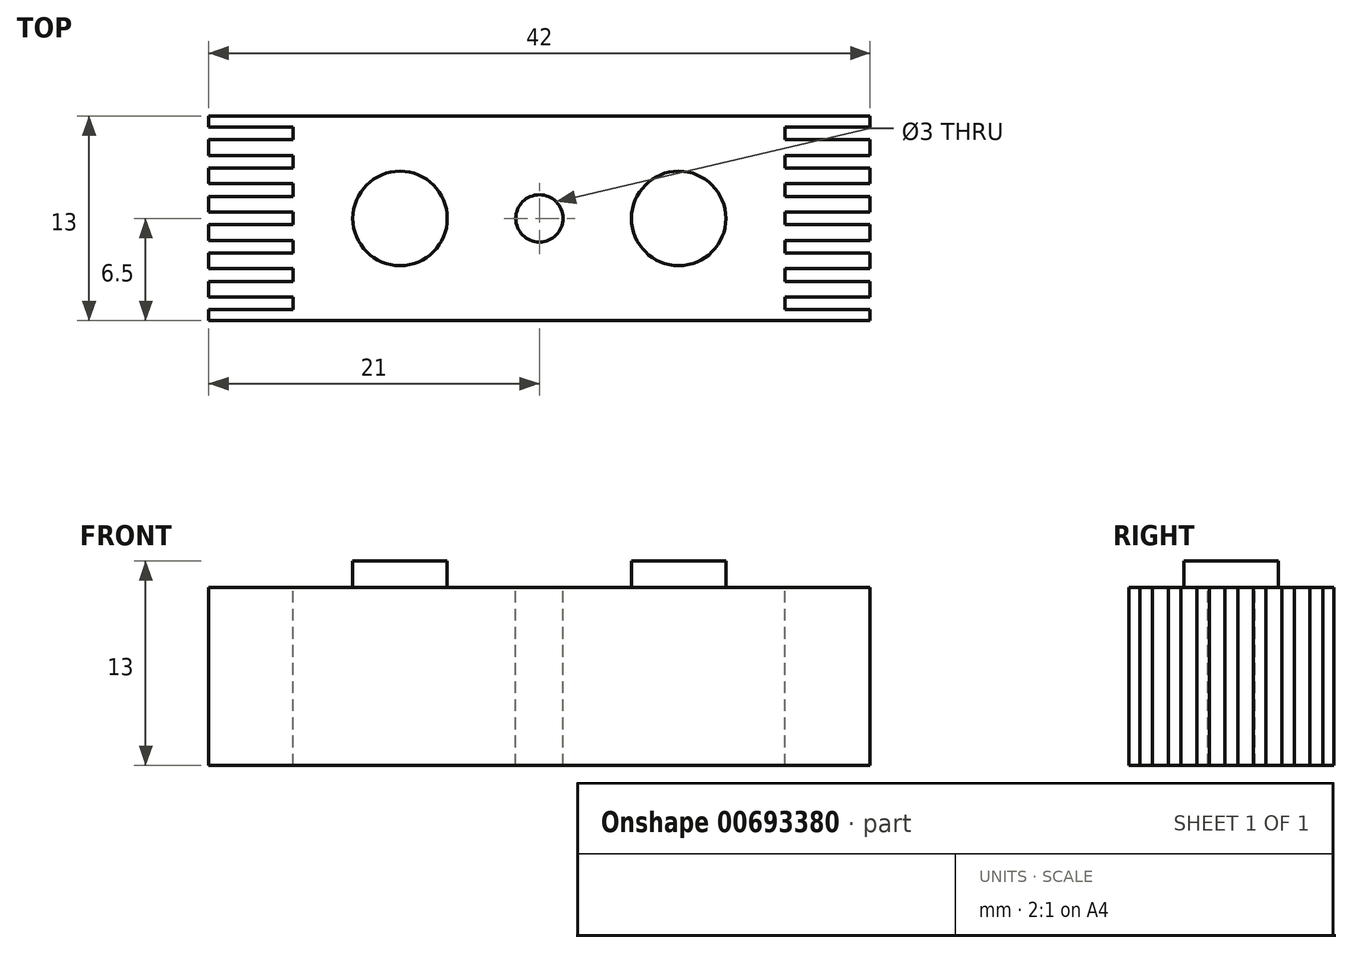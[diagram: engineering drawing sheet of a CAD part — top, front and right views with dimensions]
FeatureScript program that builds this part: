
annotation { "Feature Type Name" : "Feature", "Feature Type Description" : "" }
export const myFeature = defineFeature(function(context is Context, id is Id, definition is map)
    precondition{}
    {
        {
            var Q0;
            Q0=qCreatedBy(makeId("Top.planeOp"),FACE);
            var sketch = newSketch(context, id + "F0", { "sketchPlane" : qUnion([Q0])});
            skLineSegment(sketch, "E0.bottom", {"start": v(-21, 6.5) * mm, "end": v(21, 6.5) * mm});
            skLineSegment(sketch, "E0.top", {"start": v(-21, -6.5) * mm, "end": v(21, -6.5) * mm});
            skLineSegment(sketch, "E0.left", {"start": v(-21, 6.5) * mm, "end": v(-21, -6.5) * mm});
            skLineSegment(sketch, "E0.right", {"start": v(21, 6.5) * mm, "end": v(21, -6.5) * mm});
            skSolve(sketch);
        }
        {
            var Q0;
            Q0=makeQuery(id+"F0.imprint","IMPRINT",FACE,{"disambiguationData":[TD([[makeQuery(id+"F0.imprint","IMPRINT",EDGE,{"derivedFrom":sQuery(id+"F0.wireOp",EDGE,"E0.bottom")}),-1.0]])]});
            extrude(context, id + "F1", {"entities" : qUnion([Q0]), "depth" : 13 * mm, "offsetDistance" : 25 * mm});
        }
        {
            var Q0;
            Q0=makeQuery(id+"F1.opExtrude","CAP_FACE",FACE,{"disambiguationData":[OSD([sQuery(id+"F0.wireOp",EDGE,"E0.bottom"),sQuery(id+"F0.wireOp",EDGE,"E0.top"),sQuery(id+"F0.wireOp",EDGE,"E0.left"),sQuery(id+"F0.wireOp",EDGE,"E0.right")])],"isStart":false});
            var sketch = newSketch(context, id + "F2", { "sketchPlane" : qUnion([Q0])});
            skCircle(sketch, "E1", {"center": v(-8.85, 0) * mm, "radius": 3 * mm});
            skCircle(sketch, "E2", {"center": v(8.85, 0) * mm, "radius": 3 * mm});
            skSolve(sketch);
        }
        {
            var Q0;
            Q0=makeQuery(id+"F2.imprint","IMPRINT",FACE,{"disambiguationData":[TD([[makeQuery(id+"F2.imprint","IMPRINT",EDGE,{"derivedFrom":sQuery(id+"F2.wireOp",EDGE,"E1")}),-1.0]])]});
            extrude(context, id + "F3", {"entities" : qUnion([Q0]), "operationType" : NewBodyOperationType.REMOVE, "oppositeDirection" : true, "depth" : 1.7 * mm, "offsetDistance" : 25 * mm});
        }
        {
            var Q0;
            Q0=makeQuery(id+"F3.boolean.opBoolean","COPY",FACE,{"derivedFrom":makeQuery(id+"F3.opExtrude","CAP_FACE",FACE,{"disambiguationData":[OSD([sQuery(id+"F0.wireOp",EDGE,"E0.bottom"),sQuery(id+"F0.wireOp",EDGE,"E0.top"),sQuery(id+"F0.wireOp",EDGE,"E0.left"),sQuery(id+"F0.wireOp",EDGE,"E0.right"),sQuery(id+"F2.wireOp",EDGE,"531e28fa-9870-4099-8290-b1b5c3f36c61"),sQuery(id+"F2.wireOp",EDGE,"85907e41-ef93-42d7-a891-8f04d5f83f16"),sQuery(id+"F2.wireOp",EDGE,"5b2a0b44-cb3a-4c41-a4b0-5dba3bb4f2c2"),sQuery(id+"F2.wireOp",EDGE,"55a584b2-11a2-4efe-9052-c5b5c60a649b"),sQuery(id+"F2.wireOp",EDGE,"a54da8cc-8a24-48ef-b58d-11853cdba5fa.trimOffspring"),sQuery(id+"F2.wireOp",EDGE,"59c30cad-3298-43ef-acff-88bf1d388ae3.trimOffspring"),sQuery(id+"F2.wireOp",EDGE,"a7f2c1af-dcd8-462c-b5b2-f5b97b0a76fe.trimOffspring"),sQuery(id+"F2.wireOp",EDGE,"5d61251b-e127-4604-999b-814c6d11c452.trimOffspring")])],"isStart":false})});
            var sketch = newSketch(context, id + "F4", { "sketchPlane" : qUnion([Q0])});
            skLineSegment(sketch, "E3.bottom", {"start": v(15.6, 5.8) * mm, "end": v(21.1, 5.8) * mm});
            skLineSegment(sketch, "E3.top", {"start": v(15.6, 5) * mm, "end": v(21.1, 5) * mm});
            skLineSegment(sketch, "E3.left", {"start": v(15.6, 5.8) * mm, "end": v(15.6, 5) * mm});
            skLineSegment(sketch, "E3.right", {"start": v(21.1, 5.8) * mm, "end": v(21.1, 5) * mm});
            skLineSegment(sketch, "E4.1.0.0", {"start": v(15.6, 3.2) * mm, "end": v(21.1, 3.2) * mm});
            skLineSegment(sketch, "E4.1.0.1", {"start": v(15.6, 4) * mm, "end": v(15.6, 3.2) * mm});
            skLineSegment(sketch, "E4.1.0.2", {"start": v(21.1, 4) * mm, "end": v(21.1, 3.2) * mm});
            skLineSegment(sketch, "E4.1.0.3", {"start": v(15.6, 4) * mm, "end": v(21.1, 4) * mm});
            skLineSegment(sketch, "E4.2.0.0", {"start": v(15.6, 1.4) * mm, "end": v(21.1, 1.4) * mm});
            skLineSegment(sketch, "E4.2.0.1", {"start": v(15.6, 2.2) * mm, "end": v(15.6, 1.4) * mm});
            skLineSegment(sketch, "E4.2.0.2", {"start": v(21.1, 2.2) * mm, "end": v(21.1, 1.4) * mm});
            skLineSegment(sketch, "E4.2.0.3", {"start": v(15.6, 2.2) * mm, "end": v(21.1, 2.2) * mm});
            skLineSegment(sketch, "E4.3.0.0", {"start": v(15.6, -0.4) * mm, "end": v(21.1, -0.4) * mm});
            skLineSegment(sketch, "E4.3.0.1", {"start": v(15.6, 0.4) * mm, "end": v(15.6, -0.4) * mm});
            skLineSegment(sketch, "E4.3.0.2", {"start": v(21.1, 0.4) * mm, "end": v(21.1, -0.4) * mm});
            skLineSegment(sketch, "E4.3.0.3", {"start": v(15.6, 0.4) * mm, "end": v(21.1, 0.4) * mm});
            skLineSegment(sketch, "E4.4.0.0", {"start": v(15.6, -2.2) * mm, "end": v(21.1, -2.2) * mm});
            skLineSegment(sketch, "E4.4.0.1", {"start": v(15.6, -1.4) * mm, "end": v(15.6, -2.2) * mm});
            skLineSegment(sketch, "E4.4.0.2", {"start": v(21.1, -1.4) * mm, "end": v(21.1, -2.2) * mm});
            skLineSegment(sketch, "E4.4.0.3", {"start": v(15.6, -1.4) * mm, "end": v(21.1, -1.4) * mm});
            skLineSegment(sketch, "E4.direction1", {"start": v(15.6, 5) * mm, "end": v(15.6, 3.2) * mm, "construction": true});
            skLineSegment(sketch, "E5.0.5.0", {"start": v(15.6, -4) * mm, "end": v(21.1, -4) * mm});
            skLineSegment(sketch, "E5.3.5.0", {"start": v(15.6, -3.2) * mm, "end": v(15.6, -4) * mm});
            skLineSegment(sketch, "E5.6.5.0", {"start": v(21.1, -3.2) * mm, "end": v(21.1, -4) * mm});
            skLineSegment(sketch, "E5.9.5.0", {"start": v(15.6, -3.2) * mm, "end": v(21.1, -3.2) * mm});
            skLineSegment(sketch, "E6.0.6.0", {"start": v(15.6, -5.8) * mm, "end": v(21.1, -5.8) * mm});
            skLineSegment(sketch, "E6.3.6.0", {"start": v(15.6, -5) * mm, "end": v(15.6, -5.8) * mm});
            skLineSegment(sketch, "E6.6.6.0", {"start": v(21.1, -5) * mm, "end": v(21.1, -5.8) * mm});
            skLineSegment(sketch, "E6.9.6.0", {"start": v(15.6, -5) * mm, "end": v(21.1, -5) * mm});
            skLineSegment(sketch, "E7", {"start": v(15.6, 6.5) * mm, "end": v(15.6, -6.5) * mm});
            skLineSegment(sketch, "E8.bottom", {"start": v(-21.13, 5.8) * mm, "end": v(-15.63, 5.8) * mm});
            skLineSegment(sketch, "E8.top", {"start": v(-21.13, 5) * mm, "end": v(-15.63, 5) * mm});
            skLineSegment(sketch, "E8.left", {"start": v(-21.13, 5.8) * mm, "end": v(-21.13, 5) * mm});
            skLineSegment(sketch, "E8.right", {"start": v(-15.63, 5.8) * mm, "end": v(-15.63, 5) * mm});
            skLineSegment(sketch, "E9.1.0.0", {"start": v(-21.13, 3.2) * mm, "end": v(-15.63, 3.2) * mm});
            skLineSegment(sketch, "E9.1.0.1", {"start": v(-21.13, 4) * mm, "end": v(-21.13, 3.2) * mm});
            skLineSegment(sketch, "E9.1.0.2", {"start": v(-15.63, 4) * mm, "end": v(-15.63, 3.2) * mm});
            skLineSegment(sketch, "E9.1.0.3", {"start": v(-21.13, 4) * mm, "end": v(-15.63, 4) * mm});
            skLineSegment(sketch, "E9.2.0.0", {"start": v(-21.13, 1.4) * mm, "end": v(-15.63, 1.4) * mm});
            skLineSegment(sketch, "E9.2.0.1", {"start": v(-21.13, 2.2) * mm, "end": v(-21.13, 1.4) * mm});
            skLineSegment(sketch, "E9.2.0.2", {"start": v(-15.63, 2.2) * mm, "end": v(-15.63, 1.4) * mm});
            skLineSegment(sketch, "E9.2.0.3", {"start": v(-21.13, 2.2) * mm, "end": v(-15.63, 2.2) * mm});
            skLineSegment(sketch, "E9.3.0.0", {"start": v(-21.13, -0.4) * mm, "end": v(-15.63, -0.4) * mm});
            skLineSegment(sketch, "E9.3.0.1", {"start": v(-21.13, 0.4) * mm, "end": v(-21.13, -0.4) * mm});
            skLineSegment(sketch, "E9.3.0.2", {"start": v(-15.63, 0.4) * mm, "end": v(-15.63, -0.4) * mm});
            skLineSegment(sketch, "E9.3.0.3", {"start": v(-21.13, 0.4) * mm, "end": v(-15.63, 0.4) * mm});
            skLineSegment(sketch, "E9.4.0.0", {"start": v(-21.13, -2.2) * mm, "end": v(-15.63, -2.2) * mm});
            skLineSegment(sketch, "E9.4.0.1", {"start": v(-21.13, -1.4) * mm, "end": v(-21.13, -2.2) * mm});
            skLineSegment(sketch, "E9.4.0.2", {"start": v(-15.63, -1.4) * mm, "end": v(-15.63, -2.2) * mm});
            skLineSegment(sketch, "E9.4.0.3", {"start": v(-21.13, -1.4) * mm, "end": v(-15.63, -1.4) * mm});
            skLineSegment(sketch, "E9.direction1", {"start": v(-21.13, 5) * mm, "end": v(-21.13, 3.2) * mm, "construction": true});
            skLineSegment(sketch, "E10.0.5.0", {"start": v(-21.13, -4) * mm, "end": v(-15.63, -4) * mm});
            skLineSegment(sketch, "E10.3.5.0", {"start": v(-21.13, -3.2) * mm, "end": v(-21.13, -4) * mm});
            skLineSegment(sketch, "E10.6.5.0", {"start": v(-15.63, -3.2) * mm, "end": v(-15.63, -4) * mm});
            skLineSegment(sketch, "E10.9.5.0", {"start": v(-21.13, -3.2) * mm, "end": v(-15.63, -3.2) * mm});
            skLineSegment(sketch, "E11.0.6.0", {"start": v(-21.13, -5.8) * mm, "end": v(-15.63, -5.8) * mm});
            skLineSegment(sketch, "E11.3.6.0", {"start": v(-21.13, -5) * mm, "end": v(-21.13, -5.8) * mm});
            skLineSegment(sketch, "E11.6.6.0", {"start": v(-15.63, -5) * mm, "end": v(-15.63, -5.8) * mm});
            skLineSegment(sketch, "E11.9.6.0", {"start": v(-21.13, -5) * mm, "end": v(-15.63, -5) * mm});
            skLineSegment(sketch, "E12", {"start": v(-21.13, 6.5) * mm, "end": v(-21.13, -6.5) * mm});
            skSolve(sketch);
        }
        {
            var Q0;
            {var subQ0=sQuery(id+"F4.wireOp",EDGE,"E7");var subQ1=sQuery(id+"F4.wireOp",EDGE,"E3.bottom");var subQ2=makeQuery(id+"F4.imprint","INTERSECT",VERTEX,{"derivedFrom":[subQ1,subQ0]});Q0=makeQuery(id+"F4.imprint","IMPRINT",FACE,{"disambiguationData":[TD([[makeQuery(id+"F4.imprint","IMPRINT",EDGE,{"disambiguationData":[TD([[subQ2,-1.0]])],"derivedFrom":subQ1}),-1.0]])]});}
            var Q1;
            {var subQ0=sQuery(id+"F4.wireOp",EDGE,"E7");var subQ1=sQuery(id+"F4.wireOp",EDGE,"E4.1.0.0");var subQ2=makeQuery(id+"F4.imprint","INTERSECT",VERTEX,{"derivedFrom":[subQ1,subQ0]});Q1=makeQuery(id+"F4.imprint","IMPRINT",FACE,{"disambiguationData":[TD([[makeQuery(id+"F4.imprint","IMPRINT",EDGE,{"disambiguationData":[TD([[subQ2,-1.0]])],"derivedFrom":subQ1}),1.0]])]});}
            var Q2;
            {var subQ0=sQuery(id+"F4.wireOp",EDGE,"E7");var subQ1=sQuery(id+"F4.wireOp",EDGE,"E4.2.0.0");var subQ2=makeQuery(id+"F4.imprint","INTERSECT",VERTEX,{"derivedFrom":[subQ1,subQ0]});Q2=makeQuery(id+"F4.imprint","IMPRINT",FACE,{"disambiguationData":[TD([[makeQuery(id+"F4.imprint","IMPRINT",EDGE,{"disambiguationData":[TD([[subQ2,-1.0]])],"derivedFrom":subQ1}),1.0]])]});}
            var Q3;
            {var subQ0=sQuery(id+"F4.wireOp",EDGE,"E7");var subQ1=sQuery(id+"F4.wireOp",EDGE,"E4.3.0.0");var subQ2=makeQuery(id+"F4.imprint","INTERSECT",VERTEX,{"derivedFrom":[subQ1,subQ0]});Q3=makeQuery(id+"F4.imprint","IMPRINT",FACE,{"disambiguationData":[TD([[makeQuery(id+"F4.imprint","IMPRINT",EDGE,{"disambiguationData":[TD([[subQ2,-1.0]])],"derivedFrom":subQ1}),1.0]])]});}
            var Q4;
            {var subQ0=sQuery(id+"F4.wireOp",EDGE,"E7");var subQ1=sQuery(id+"F4.wireOp",EDGE,"E4.4.0.0");var subQ2=makeQuery(id+"F4.imprint","INTERSECT",VERTEX,{"derivedFrom":[subQ1,subQ0]});Q4=makeQuery(id+"F4.imprint","IMPRINT",FACE,{"disambiguationData":[TD([[makeQuery(id+"F4.imprint","IMPRINT",EDGE,{"disambiguationData":[TD([[subQ2,-1.0]])],"derivedFrom":subQ1}),1.0]])]});}
            var Q5;
            {var subQ0=sQuery(id+"F4.wireOp",EDGE,"E7");var subQ1=sQuery(id+"F4.wireOp",EDGE,"E5.0.5.0");var subQ2=makeQuery(id+"F4.imprint","INTERSECT",VERTEX,{"derivedFrom":[subQ1,subQ0]});Q5=makeQuery(id+"F4.imprint","IMPRINT",FACE,{"disambiguationData":[TD([[makeQuery(id+"F4.imprint","IMPRINT",EDGE,{"disambiguationData":[TD([[subQ2,-1.0]])],"derivedFrom":subQ1}),1.0]])]});}
            var Q6;
            {var subQ0=sQuery(id+"F4.wireOp",EDGE,"E7");var subQ1=sQuery(id+"F4.wireOp",EDGE,"E6.0.6.0");var subQ2=makeQuery(id+"F4.imprint","INTERSECT",VERTEX,{"derivedFrom":[subQ1,subQ0]});Q6=makeQuery(id+"F4.imprint","IMPRINT",FACE,{"disambiguationData":[TD([[makeQuery(id+"F4.imprint","IMPRINT",EDGE,{"disambiguationData":[TD([[subQ2,-1.0]])],"derivedFrom":subQ1}),1.0]])]});}
            var Q7;
            {var subQ0=sQuery(id+"F4.wireOp",EDGE,"E8.right");Q7=makeQuery(id+"F4.imprint","IMPRINT",FACE,{"disambiguationData":[TD([[makeQuery(id+"F4.imprint","IMPRINT",EDGE,{"derivedFrom":subQ0}),-1.0]])]});}
            var Q8;
            {var subQ0=sQuery(id+"F4.wireOp",EDGE,"E9.1.0.2");Q8=makeQuery(id+"F4.imprint","IMPRINT",FACE,{"disambiguationData":[TD([[makeQuery(id+"F4.imprint","IMPRINT",EDGE,{"derivedFrom":subQ0}),-1.0]])]});}
            var Q9;
            {var subQ0=sQuery(id+"F4.wireOp",EDGE,"E9.2.0.2");Q9=makeQuery(id+"F4.imprint","IMPRINT",FACE,{"disambiguationData":[TD([[makeQuery(id+"F4.imprint","IMPRINT",EDGE,{"derivedFrom":subQ0}),-1.0]])]});}
            var Q10;
            {var subQ0=sQuery(id+"F4.wireOp",EDGE,"E9.3.0.2");Q10=makeQuery(id+"F4.imprint","IMPRINT",FACE,{"disambiguationData":[TD([[makeQuery(id+"F4.imprint","IMPRINT",EDGE,{"derivedFrom":subQ0}),-1.0]])]});}
            var Q11;
            {var subQ0=sQuery(id+"F4.wireOp",EDGE,"E9.4.0.2");Q11=makeQuery(id+"F4.imprint","IMPRINT",FACE,{"disambiguationData":[TD([[makeQuery(id+"F4.imprint","IMPRINT",EDGE,{"derivedFrom":subQ0}),-1.0]])]});}
            var Q12;
            {var subQ0=sQuery(id+"F4.wireOp",EDGE,"E10.6.5.0");Q12=makeQuery(id+"F4.imprint","IMPRINT",FACE,{"disambiguationData":[TD([[makeQuery(id+"F4.imprint","IMPRINT",EDGE,{"derivedFrom":subQ0}),-1.0]])]});}
            var Q13;
            {var subQ0=sQuery(id+"F4.wireOp",EDGE,"E11.6.6.0");Q13=makeQuery(id+"F4.imprint","IMPRINT",FACE,{"disambiguationData":[TD([[makeQuery(id+"F4.imprint","IMPRINT",EDGE,{"derivedFrom":subQ0}),-1.0]])]});}
            extrude(context, id + "F5", {"entities" : qUnion([Q0, Q1, Q2, Q3, Q4, Q5, Q6, Q7, Q8, Q9, Q10, Q11, Q12, Q13]), "operationType" : NewBodyOperationType.REMOVE, "endBound" : BoundingType.THROUGH_ALL, "oppositeDirection" : true, "depth" : 25 * mm, "offsetDistance" : 25 * mm});
        }
        {
            var Q0;
            Q0=makeQuery(id+"F3.boolean.opBoolean","COPY",FACE,{"derivedFrom":makeQuery(id+"F3.opExtrude","CAP_FACE",FACE,{"disambiguationData":[OSD([sQuery(id+"F0.wireOp",EDGE,"E0.bottom"),sQuery(id+"F0.wireOp",EDGE,"E0.top"),sQuery(id+"F0.wireOp",EDGE,"E0.left"),sQuery(id+"F0.wireOp",EDGE,"E0.right"),sQuery(id+"F2.wireOp",EDGE,"531e28fa-9870-4099-8290-b1b5c3f36c61"),sQuery(id+"F2.wireOp",EDGE,"85907e41-ef93-42d7-a891-8f04d5f83f16"),sQuery(id+"F2.wireOp",EDGE,"5b2a0b44-cb3a-4c41-a4b0-5dba3bb4f2c2"),sQuery(id+"F2.wireOp",EDGE,"55a584b2-11a2-4efe-9052-c5b5c60a649b"),sQuery(id+"F2.wireOp",EDGE,"a54da8cc-8a24-48ef-b58d-11853cdba5fa.trimOffspring"),sQuery(id+"F2.wireOp",EDGE,"59c30cad-3298-43ef-acff-88bf1d388ae3.trimOffspring"),sQuery(id+"F2.wireOp",EDGE,"a7f2c1af-dcd8-462c-b5b2-f5b97b0a76fe.trimOffspring"),sQuery(id+"F2.wireOp",EDGE,"5d61251b-e127-4604-999b-814c6d11c452.trimOffspring")])],"isStart":false})});
            var sketch = newSketch(context, id + "F6", { "sketchPlane" : qUnion([Q0])});
            skSolve(sketch);
        }
        {
            var Q0;
            {var subQ27=sQuery(id+"F2.wireOp",EDGE,"E1");Q0=makeQuery(id+"F6.imprint","IMPRINT",FACE,{"disambiguationData":[TD([[makeQuery(id+"F6.imprint","IMPRINT",EDGE,{"derivedFrom":makeQuery(id+"F3.boolean.opBoolean","COPY",EDGE,{"derivedFrom":makeQuery(id+"F3.opExtrude","CAP_EDGE",EDGE,{"disambiguationData":[OSD([subQ27])],"isStart":false})})}),-1.0]])]});}
            var sketch = newSketch(context, id + "F7", { "sketchPlane" : qUnion([Q0])});
            skCircle(sketch, "E13", {"center": v(0, 0) * mm, "radius": 1.5 * mm});
            skSolve(sketch);
        }
        {
            var Q0;
            Q0=qSketchRegion(id+"F7",true);
            extrude(context, id + "F8", {"entities" : qUnion([Q0]), "operationType" : NewBodyOperationType.REMOVE, "endBound" : BoundingType.THROUGH_ALL, "oppositeDirection" : true, "depth" : 5 * mm, "offsetDistance" : 25 * mm});
        }
    });
